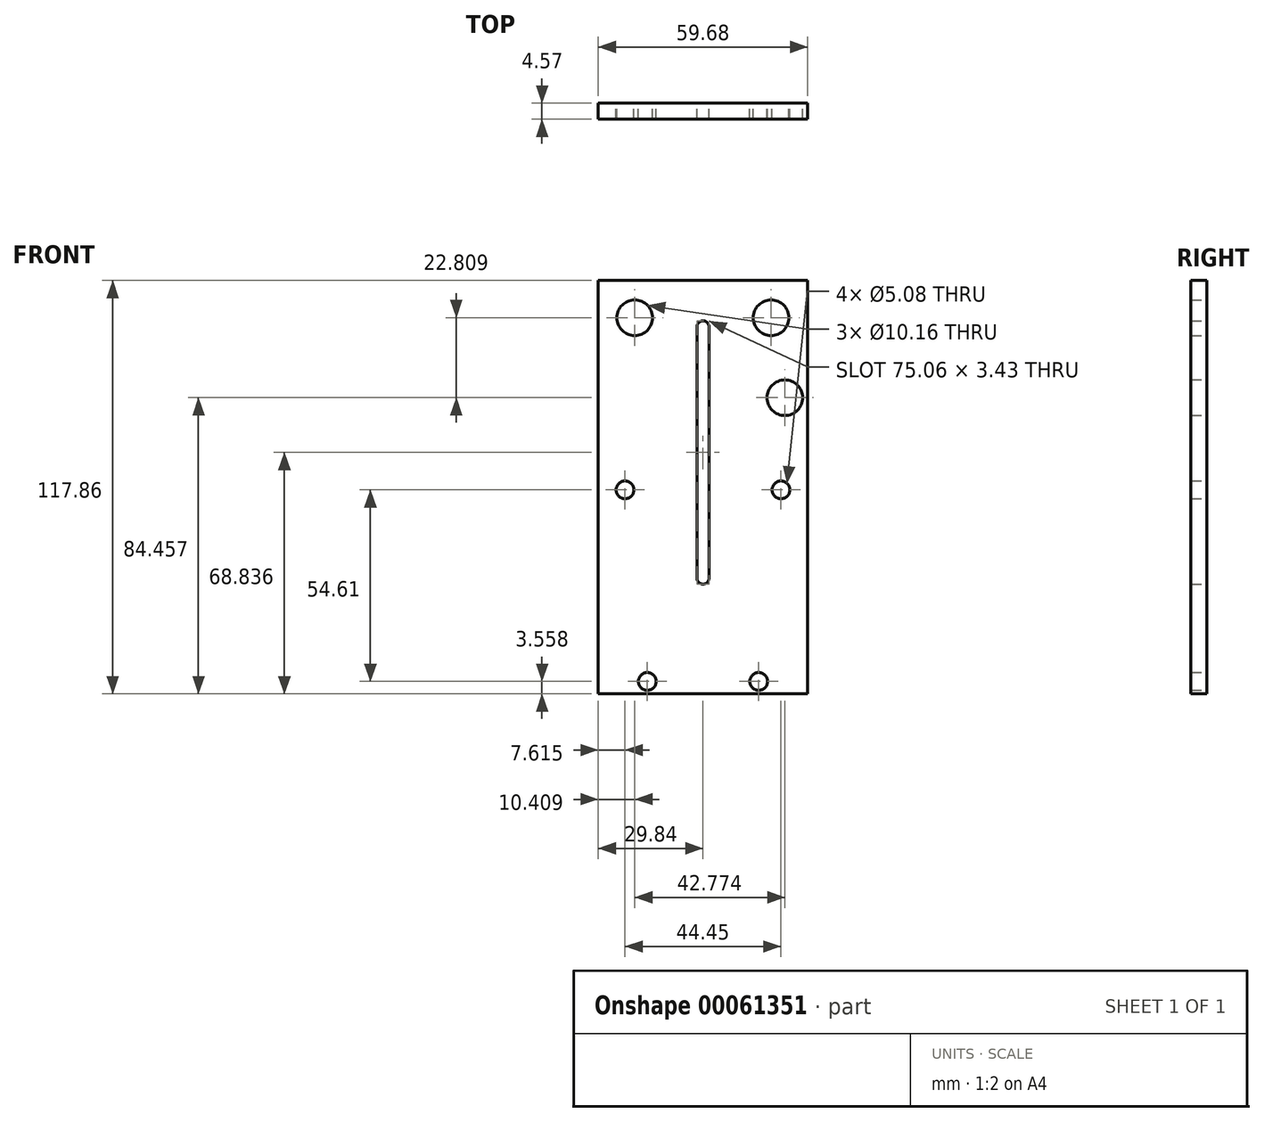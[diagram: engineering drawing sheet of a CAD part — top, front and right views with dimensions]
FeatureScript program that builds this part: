
annotation { "Feature Type Name" : "Feature", "Feature Type Description" : "" }
export const myFeature = defineFeature(function(context is Context, id is Id, definition is map)
    precondition{}
    {
        {
            var Q0;
            Q0=qCreatedBy(makeId("Front.planeOp"),FACE);
            var sketch = newSketch(context, id + "F0", { "sketchPlane" : qUnion([Q0])});
            skLineSegment(sketch, "E0.rect.bottom", {"start": v(-29.84, 58.93) * mm, "end": v(29.85, 58.93) * mm});
            skLineSegment(sketch, "E0.rect.top", {"start": v(-29.85, -58.93) * mm, "end": v(29.84, -58.93) * mm});
            skLineSegment(sketch, "E0.rect.left", {"start": v(-29.84, 58.93) * mm, "end": v(-29.85, -58.93) * mm});
            skLineSegment(sketch, "E0.rect.right", {"start": v(29.85, 58.93) * mm, "end": v(29.84, -58.93) * mm});
            skPoint(sketch, "E0.rect.middle", {"position": v(0, 0) * mm});
            skPoint(sketch, "E1", {"position": v(-19.43, 48.34) * mm});
            skPoint(sketch, "E2", {"position": v(19.43, 48.34) * mm});
            skPoint(sketch, "E3", {"position": v(-22.23, -0.76) * mm});
            skPoint(sketch, "E4", {"position": v(22.23, -0.76) * mm});
            skPoint(sketch, "E5", {"position": v(-15.87, -55.37) * mm});
            skPoint(sketch, "E6", {"position": v(15.88, -55.37) * mm});
            skPoint(sketch, "E7", {"position": v(0, 45.72) * mm});
            skPoint(sketch, "E8", {"position": v(0, -25.9) * mm});
            skPoint(sketch, "E9", {"position": v(23.34, 25.53) * mm});
            skArc(sketch, "E10", {"start": v(1.71, 45.72) * mm, "mid": v(0, 47.43) * mm, "end": v(-1.71, 45.72) * mm});
            skArc(sketch, "E11", {"start": v(-1.71, -25.9) * mm, "mid": v(0, -27.62) * mm, "end": v(1.71, -25.9) * mm});
            skLineSegment(sketch, "E12", {"start": v(-1.71, 45.72) * mm, "end": v(-1.71, -25.9) * mm});
            skLineSegment(sketch, "E13", {"start": v(1.71, -25.9) * mm, "end": v(1.71, 45.72) * mm});
            skSolve(sketch);
        }
        {
            var Q0;
            Q0 = qSketchRegion(id + "F0", true);
            extrude(context, id + "F1", {"entities" : qUnion([Q0]), "depth" : 4.57 * mm});
        }
        {
            var Q0;
            Q0=sQuery(id+"F0.wireOp",VERTEX,"E1");
            var Q1;
            Q1=sQuery(id+"F0.wireOp",VERTEX,"E2");
            var Q2;
            Q2=sQuery(id+"F0.wireOp",VERTEX,"E9");
            var Q3;
            Q3=makeQuery(id+"F1.opExtrude","SWEPT_BODY",BODY,{"disambiguationData":[OSD([sQuery(id+"F0.wireOp",EDGE,"E0.rect.bottom"),sQuery(id+"F0.wireOp",EDGE,"E0.rect.top"),sQuery(id+"F0.wireOp",EDGE,"E0.rect.left"),sQuery(id+"F0.wireOp",EDGE,"E0.rect.right")])]});
            hole(context, id + "F2", {"style" : HoleStyle.SIMPLE, "holeDiameter" : 10.16 * mm, "endStyle" : HoleEndStyle.THROUGH, "oppositeDirection" : true, "locations" : qUnion([Q0, Q1, Q2]), "scope" : qUnion([Q3])});
        }
        {
            var Q0;
            Q0=sQuery(id+"F0.wireOp",VERTEX,"E3");
            var Q1;
            Q1=sQuery(id+"F0.wireOp",VERTEX,"E4");
            var Q2;
            Q2=sQuery(id+"F0.wireOp",VERTEX,"E5");
            var Q3;
            Q3=sQuery(id+"F0.wireOp",VERTEX,"E6");
            var Q4;
            Q4=makeQuery(id+"F1.opExtrude","SWEPT_BODY",BODY,{"disambiguationData":[OSD([sQuery(id+"F0.wireOp",EDGE,"E0.rect.bottom"),sQuery(id+"F0.wireOp",EDGE,"E0.rect.top"),sQuery(id+"F0.wireOp",EDGE,"E0.rect.left"),sQuery(id+"F0.wireOp",EDGE,"E0.rect.right")])]});
            hole(context, id + "F3", {"style" : HoleStyle.SIMPLE, "holeDiameter" : 5.08 * mm, "endStyle" : HoleEndStyle.THROUGH, "oppositeDirection" : true, "locations" : qUnion([Q0, Q1, Q2, Q3]), "scope" : qUnion([Q4])});
        }
    });
